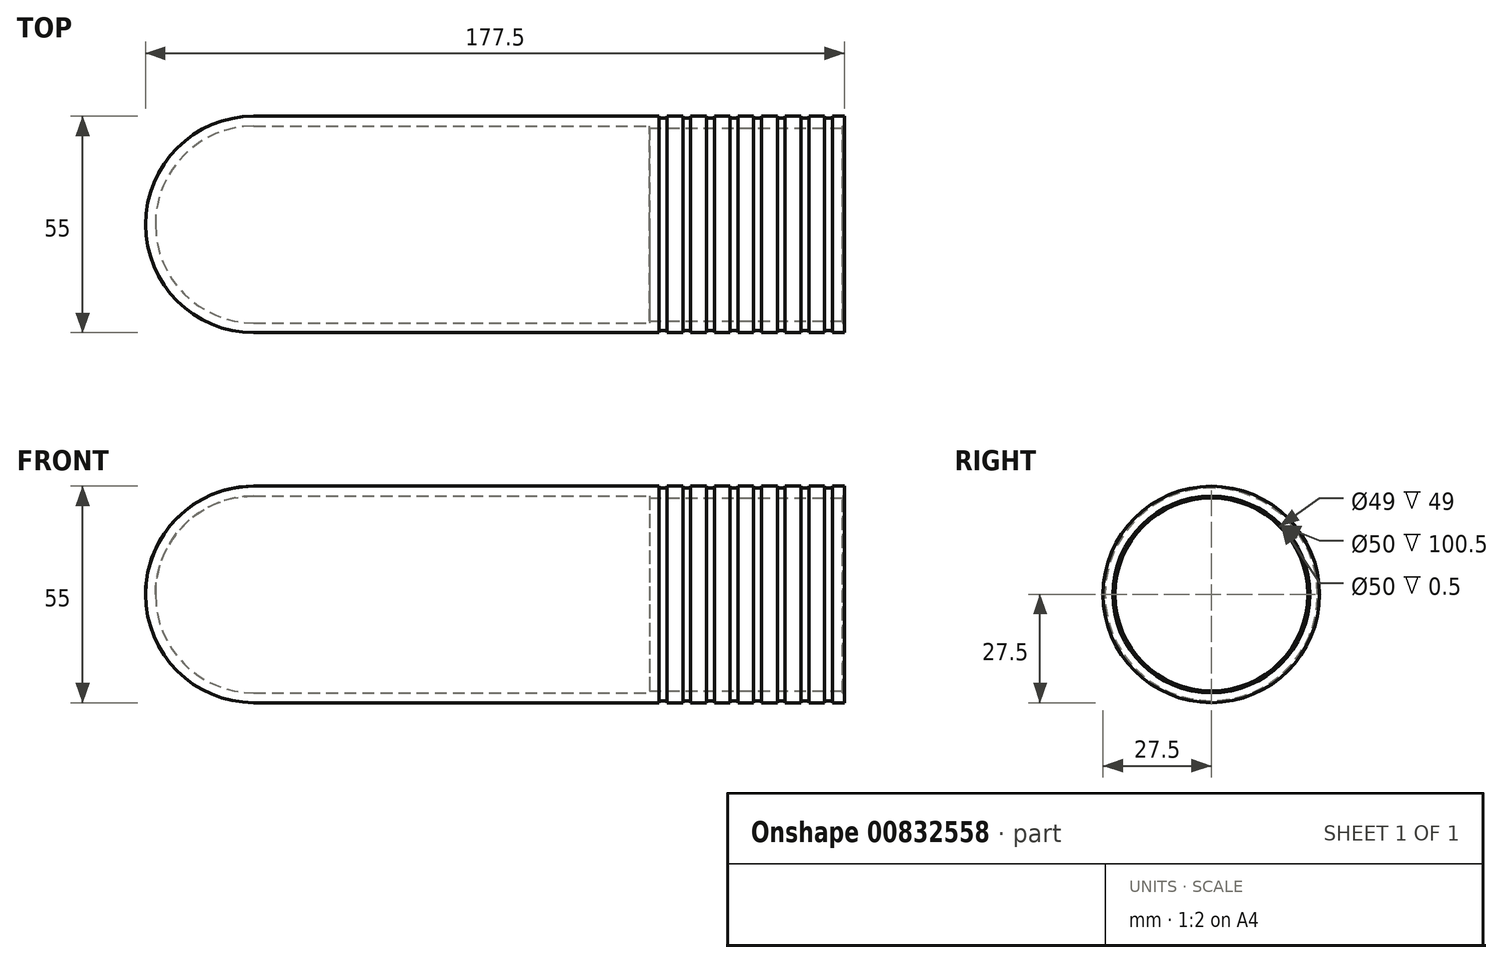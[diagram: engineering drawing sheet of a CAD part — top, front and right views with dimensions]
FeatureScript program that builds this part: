
annotation { "Feature Type Name" : "Feature", "Feature Type Description" : "" }
export const myFeature = defineFeature(function(context is Context, id is Id, definition is map)
    precondition{}
    {
        {
            var Q0;
            Q0=qCreatedBy(makeId("Front.planeOp"),FACE);
            var sketch = newSketch(context, id + "F0", { "sketchPlane" : qUnion([Q0])});
            skLineSegment(sketch, "E0", {"start": v(81.05, 0) * mm, "end": v(81.05, 27.5) * mm});
            skLineSegment(sketch, "E1", {"start": v(81.05, 27.5) * mm, "end": v(78.05, 27.5) * mm});
            skLineSegment(sketch, "E2", {"start": v(-68.95, 27.5) * mm, "end": v(-68.95, 27.5) * mm});
            skArc(sketch, "E3", {"start": v(-68.95, 27.5) * mm, "mid": v(-88.4, 19.45) * mm, "end": v(-96.45, 0) * mm});
            skLineSegment(sketch, "E4", {"start": v(81.05, 0) * mm, "end": v(-96.45, 0) * mm});
            skLineSegment(sketch, "E5", {"start": v(78.05, 27.5) * mm, "end": v(78.05, 27) * mm});
            skLineSegment(sketch, "E6.0", {"start": v(76.05, 27.5) * mm, "end": v(76.05, 27) * mm});
            skLineSegment(sketch, "E7.0", {"start": v(72.05, 27.5) * mm, "end": v(72.05, 27) * mm});
            skLineSegment(sketch, "E8.0", {"start": v(70.05, 27.5) * mm, "end": v(70.05, 27) * mm});
            skLineSegment(sketch, "E9.0", {"start": v(66.05, 27.5) * mm, "end": v(66.05, 27) * mm});
            skLineSegment(sketch, "E10.0", {"start": v(64.05, 27.5) * mm, "end": v(64.05, 27) * mm});
            skLineSegment(sketch, "E11.0", {"start": v(60.05, 27.5) * mm, "end": v(60.05, 27) * mm});
            skLineSegment(sketch, "E12.0", {"start": v(58.05, 27.5) * mm, "end": v(58.05, 27) * mm});
            skLineSegment(sketch, "E13.0", {"start": v(54.05, 27.5) * mm, "end": v(54.05, 27) * mm});
            skLineSegment(sketch, "E14.0", {"start": v(52.05, 27.5) * mm, "end": v(52.05, 27) * mm});
            skLineSegment(sketch, "E15.trimOffspring", {"start": v(58.05, 27.5) * mm, "end": v(54.05, 27.5) * mm});
            skLineSegment(sketch, "E16.trimOffspring", {"start": v(64.05, 27.5) * mm, "end": v(60.05, 27.5) * mm});
            skLineSegment(sketch, "E17.trimOffspring", {"start": v(70.05, 27.5) * mm, "end": v(66.05, 27.5) * mm});
            skLineSegment(sketch, "E18.trimOffspring", {"start": v(76.05, 27.5) * mm, "end": v(72.05, 27.5) * mm});
            skLineSegment(sketch, "E19.trimOffspring", {"start": v(52.05, 27) * mm, "end": v(54.05, 27) * mm});
            skLineSegment(sketch, "E20.trimOffspring", {"start": v(58.05, 27) * mm, "end": v(60.05, 27) * mm});
            skLineSegment(sketch, "E21.trimOffspring", {"start": v(64.05, 27) * mm, "end": v(66.05, 27) * mm});
            skLineSegment(sketch, "E22.trimOffspring", {"start": v(70.05, 27) * mm, "end": v(72.05, 27) * mm});
            skLineSegment(sketch, "E23.trimOffspring", {"start": v(76.05, 27) * mm, "end": v(78.05, 27) * mm});
            skPoint(sketch, "E24.trimOffspring.end.orphan", {"position": v(63.12, 26) * mm});
            skPoint(sketch, "E25.orphan", {"position": v(78.05, 0) * mm});
            skLineSegment(sketch, "E26.trimOffspring", {"start": v(46.05, 27.5) * mm, "end": v(42.05, 27.5) * mm});
            skLineSegment(sketch, "E27.trimOffspring", {"start": v(34.05, 27.5) * mm, "end": v(25.05, 27.5) * mm});
            skLineSegment(sketch, "E28.0", {"start": v(48.05, 27.5) * mm, "end": v(48.05, 27) * mm});
            skLineSegment(sketch, "E29.0", {"start": v(46.05, 27.5) * mm, "end": v(46.05, 27) * mm});
            skLineSegment(sketch, "E30.0", {"start": v(42.05, 27.5) * mm, "end": v(42.05, 27) * mm});
            skLineSegment(sketch, "E31.0", {"start": v(40.05, 27.5) * mm, "end": v(40.05, 27) * mm});
            skLineSegment(sketch, "E32.0", {"start": v(36.05, 27.5) * mm, "end": v(36.05, 27) * mm});
            skLineSegment(sketch, "E33", {"start": v(34.05, 27.5) * mm, "end": v(32.05, 27.5) * mm});
            skLineSegment(sketch, "E34", {"start": v(48.05, 27) * mm, "end": v(46.05, 27) * mm});
            skLineSegment(sketch, "E35.trimOffspring", {"start": v(42.05, 27) * mm, "end": v(40.05, 27) * mm});
            skLineSegment(sketch, "E36.trimOffspring", {"start": v(40.05, 27.5) * mm, "end": v(36.05, 27.5) * mm});
            skLineSegment(sketch, "E37.0", {"start": v(34.05, 27.5) * mm, "end": v(34.05, 27) * mm});
            skLineSegment(sketch, "E38", {"start": v(36.05, 27) * mm, "end": v(34.05, 27) * mm});
            skLineSegment(sketch, "E39.trimOffspring", {"start": v(34.05, 27.5) * mm, "end": v(-68.95, 27.5) * mm});
            skLineSegment(sketch, "E40.trimOffspring", {"start": v(56.05, 27.5) * mm, "end": v(54.05, 27.5) * mm});
            skLineSegment(sketch, "E41.trimOffspring", {"start": v(52.05, 27.5) * mm, "end": v(48.05, 27.5) * mm});
            skSolve(sketch);
        }
        {
            var Q0;
            Q0=makeQuery(id+"F0.imprint","IMPRINT",FACE,{"disambiguationData":[TD([[makeQuery(id+"F0.imprint","IMPRINT",EDGE,{"derivedFrom":sQuery(id+"F0.wireOp",EDGE,"E0")}),1.0]])]});
            var Q1;
            Q1=sQuery(id+"F0.wireOp",EDGE,"E4");
            revolve(context, id + "F1", {"surfaceOperationType" : NewSurfaceOperationType.NEW, "entities" : qUnion([Q0]), "axis" : qUnion([Q1]), "revolveType" : RevolveType.FULL});
        }
        {
            var Q0;
            Q0=makeQuery(id+"F1.opRevolve","SWEPT_FACE",FACE,{"disambiguationData":[OSD([sQuery(id+"F0.wireOp",EDGE,"E0")])]});
            shell(context, id + "F2", {"entities" : qUnion([Q0]), "thickness" : 2.5 * mm});
        }
    });
